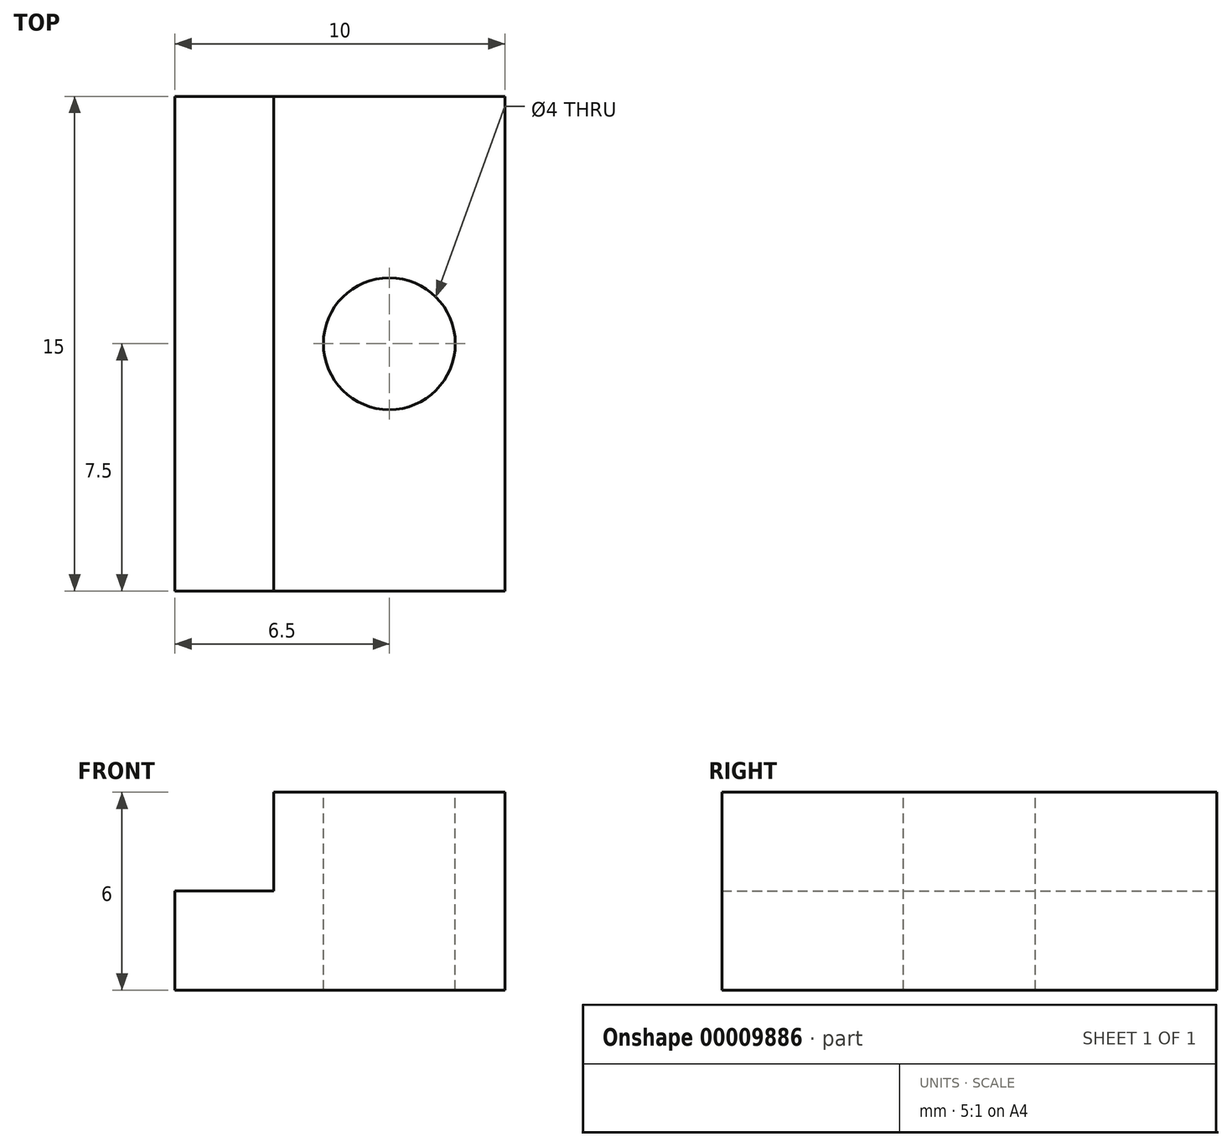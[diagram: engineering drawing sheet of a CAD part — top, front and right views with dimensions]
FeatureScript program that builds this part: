
annotation { "Feature Type Name" : "Feature", "Feature Type Description" : "" }
export const myFeature = defineFeature(function(context is Context, id is Id, definition is map)
    precondition{}
    {
        {
            var Q0;
            Q0=qCreatedBy(makeId("Top.planeOp"),FACE);
            var sketch = newSketch(context, id + "F0", { "sketchPlane" : qUnion([Q0])});
            skLineSegment(sketch, "E0.bottom", {"start": v(0, 0) * mm, "end": v(10, 0) * mm});
            skLineSegment(sketch, "E0.top", {"start": v(0, 15) * mm, "end": v(10, 15) * mm});
            skLineSegment(sketch, "E0.left", {"start": v(0, 0) * mm, "end": v(0, 15) * mm});
            skLineSegment(sketch, "E0.right", {"start": v(10, 0) * mm, "end": v(10, 15) * mm});
            skSolve(sketch);
        }
        {
            var Q0;
            Q0 = qSketchRegion(id + "F0", true);
            extrude(context, id + "F1", {"entities" : qUnion([Q0]), "depth" : 6 * mm});
        }
        {
            var Q0;
            Q0=makeQuery(id+"F1.opExtrude","CAP_FACE",FACE,{"disambiguationData":[OSD([sQuery(id+"F0.wireOp",EDGE,"E0.bottom"),sQuery(id+"F0.wireOp",EDGE,"E0.top"),sQuery(id+"F0.wireOp",EDGE,"E0.left"),sQuery(id+"F0.wireOp",EDGE,"E0.right")])],"isStart":false});
            var sketch = newSketch(context, id + "F2", { "sketchPlane" : qUnion([Q0])});
            skLineSegment(sketch, "E1.bottom", {"start": v(0, 15) * mm, "end": v(3, 15) * mm});
            skLineSegment(sketch, "E1.top", {"start": v(0, 0) * mm, "end": v(3, 0) * mm});
            skLineSegment(sketch, "E1.left", {"start": v(0, 15) * mm, "end": v(0, 0) * mm});
            skLineSegment(sketch, "E1.right", {"start": v(3, 15) * mm, "end": v(3, 0) * mm});
            skSolve(sketch);
        }
        {
            var Q0;
            Q0 = qSketchRegion(id + "F2", true);
            extrude(context, id + "F3", {"entities" : qUnion([Q0]), "operationType" : NewBodyOperationType.REMOVE, "oppositeDirection" : true, "depth" : 3 * mm});
        }
        {
            var Q0;
            Q0=makeQuery(id+"F1.opExtrude","CAP_FACE",FACE,{"disambiguationData":[OSD([sQuery(id+"F0.wireOp",EDGE,"E0.bottom"),sQuery(id+"F0.wireOp",EDGE,"E0.top"),sQuery(id+"F0.wireOp",EDGE,"E0.left"),sQuery(id+"F0.wireOp",EDGE,"E0.right")])],"isStart":false});
            var sketch = newSketch(context, id + "F4", { "sketchPlane" : qUnion([Q0])});
            skCircle(sketch, "E2", {"center": v(6.5, 7.5) * mm, "radius": 2 * mm});
            skPoint(sketch, "E3", {"position": v(6.5, 15) * mm});
            skPoint(sketch, "E4", {"position": v(10, 7.5) * mm});
            skSolve(sketch);
        }
        {
            var Q0;
            Q0 = qSketchRegion(id + "F4", true);
            extrude(context, id + "F5", {"entities" : qUnion([Q0]), "operationType" : NewBodyOperationType.REMOVE, "oppositeDirection" : true, "depth" : 25 * mm});
        }
    });
